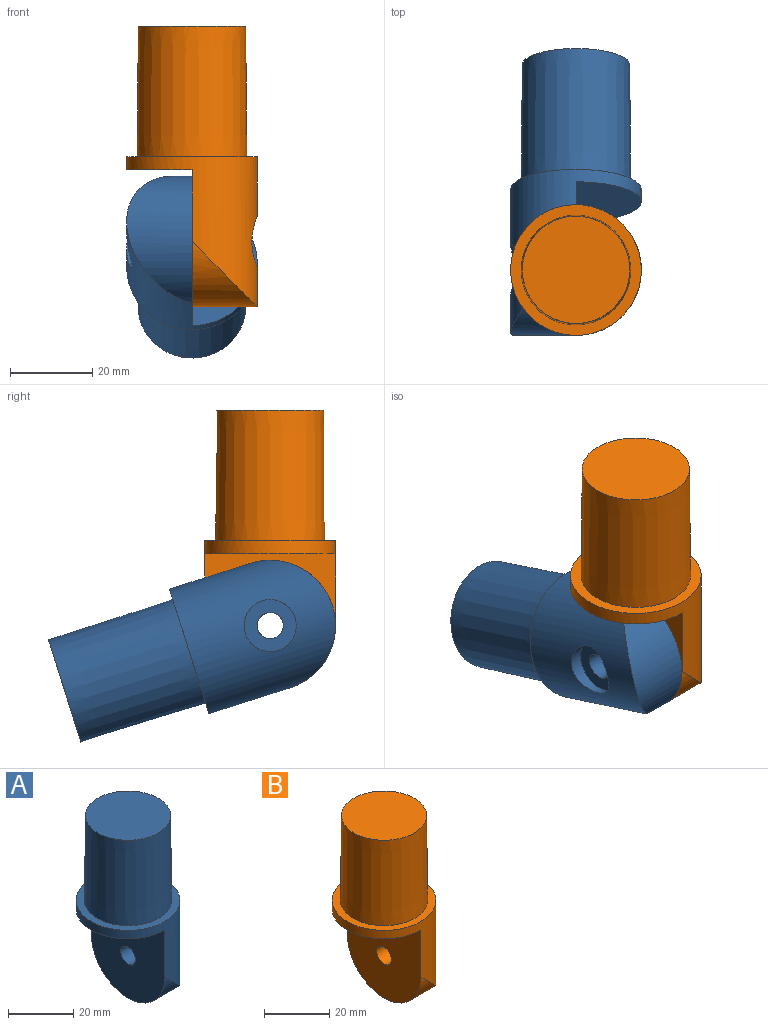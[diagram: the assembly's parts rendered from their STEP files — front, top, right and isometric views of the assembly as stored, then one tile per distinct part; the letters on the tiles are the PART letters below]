
ASSEMBLY  parts=2 mates=1
PART A: 10 faces, bbox 31.8x31.8x68.3 mm
  f0: cylinder r=3.17mm len=12.7mm, axis (-1,0,0), area 253.4mm2, adj f1,f8
  f1: plane 33.34x31.75mm, normal (-1,0,0), area 918.6mm2, adj f0,f2,f6,f7
  f2: cylinder r=15.88mm len=36.51mm, axis (0,0,1), area 1562.1mm2, adj f1,f5,f6,f7,f9
  f3: cone r=13.32mm half-angle=0.5deg, axis (0,0,-1), area 2630.1mm2, adj f4,f5
  f4: plane 26.09x26.09mm, normal (0,0,1), area 534.6mm2, adj f3
  f5: plane 31.75x31.75mm, normal (0,0,1), area 234.1mm2, adj f2,f3
  f6: plane 31.75x15.88mm, normal (0,0,-1), area 395.9mm2, adj f1,f2
  f7: cylinder r=15.88mm len=31.75mm, axis (-1,0,0), area 504mm2, adj f1,f2
  f8: plane 12.7x12.7mm, normal (1,0,0), area 95mm2, adj f0,f9
  f9: cylinder r=6.35mm len=12.7mm, axis (1,0,0), area 100.5mm2, adj f2,f8
PART B: 10 faces, bbox 31.8x31.8x68.3 mm
  f0: cylinder r=3.17mm len=8.06mm, axis (-1,0,0), area 160.9mm2, adj f1,f8
  f1: plane 33.34x31.75mm, normal (-1,0,0), area 918.6mm2, adj f0,f2,f6,f7
  f2: cylinder r=15.88mm len=36.51mm, axis (0,0,1), area 1562.1mm2, adj f1,f5,f6,f7,f9
  f3: cone r=13.32mm half-angle=0.5deg, axis (0,0,-1), area 2630.1mm2, adj f4,f5
  f4: plane 26.09x26.09mm, normal (0,0,1), area 534.6mm2, adj f3
  f5: plane 31.75x31.75mm, normal (0,0,1), area 234.1mm2, adj f2,f3
  f6: plane 31.75x15.88mm, normal (0,0,-1), area 395.9mm2, adj f1,f2
  f7: cylinder r=15.88mm len=31.75mm, axis (-1,0,0), area 504mm2, adj f1,f2
  f8: plane 12.7x12.7mm, normal (1,0,0), area 95mm2, adj f0,f9
  f9: cylinder r=6.35mm len=12.7mm, axis (1,0,0), area 285.5mm2, adj f2,f8
PLACE A rot(axis=(0,-0.81,-0.59),180deg) t=(-30.82,-48.06,-74.58)mm
PLACE B t=(-30.82,-67.73,-47.69)mm
MATE revolute A.f0 <-> B.f0  axis (1,0,0) through (-30.82,-67.73,-68.33)mm
